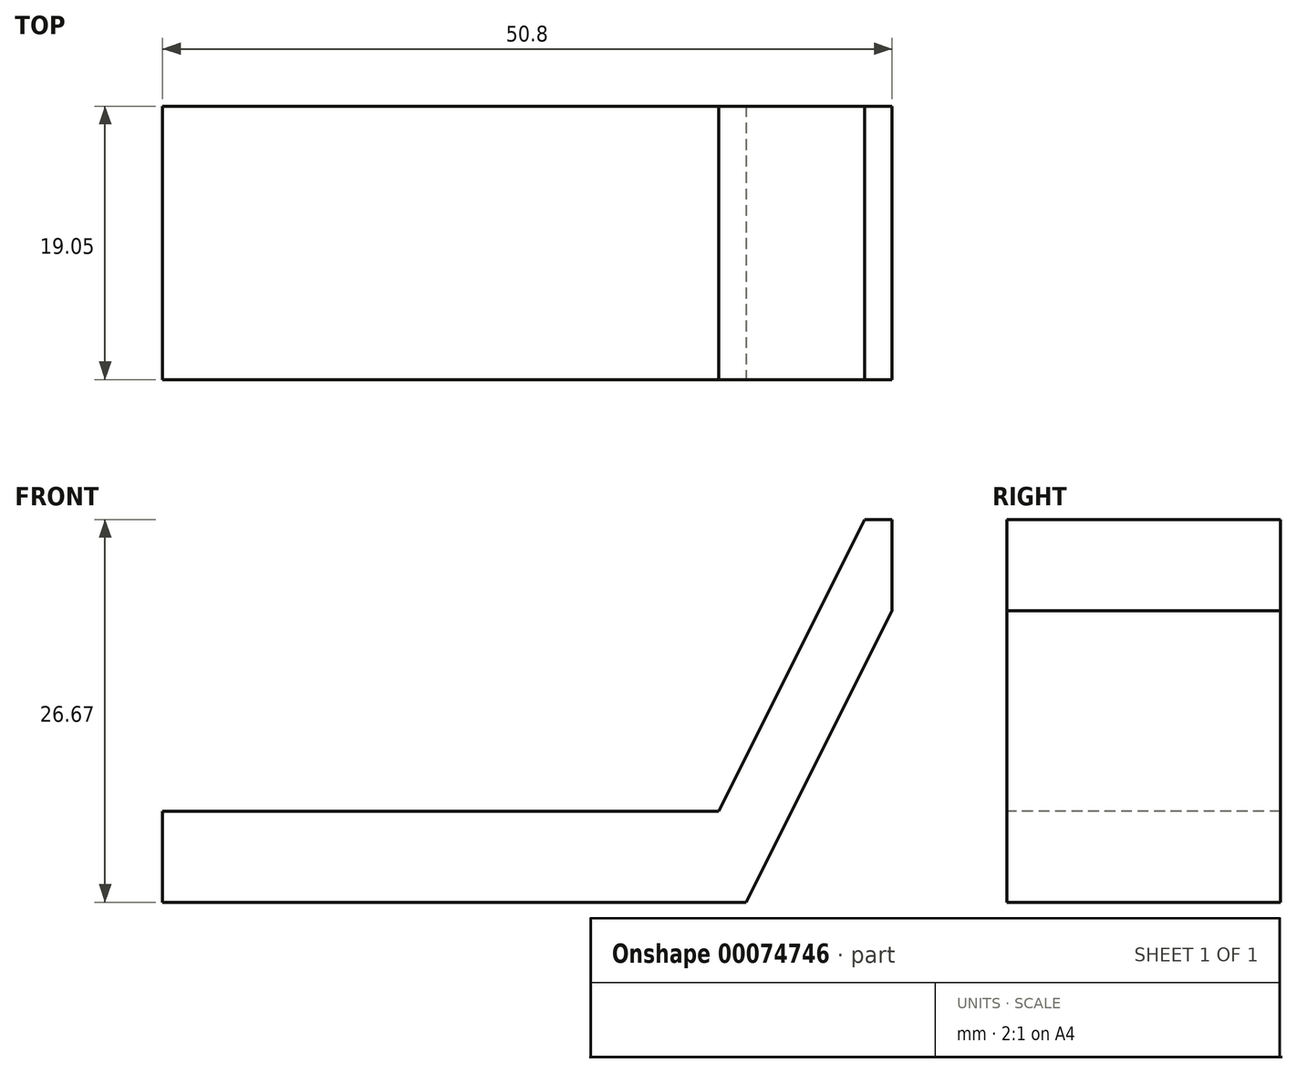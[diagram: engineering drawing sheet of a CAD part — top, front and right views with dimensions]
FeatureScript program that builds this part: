
annotation { "Feature Type Name" : "Feature", "Feature Type Description" : "" }
export const myFeature = defineFeature(function(context is Context, id is Id, definition is map)
    precondition{}
    {
        {
            var Q0;
            Q0=qCreatedBy(makeId("Front.planeOp"),FACE);
            var sketch = newSketch(context, id + "F0", { "sketchPlane" : qUnion([Q0])});
            skLineSegment(sketch, "E0", {"start": v(0, 0) * mm, "end": v(50.8, 0) * mm});
            skLineSegment(sketch, "E1", {"start": v(50.8, 0) * mm, "end": v(50.8, -6.35) * mm});
            skLineSegment(sketch, "E2", {"start": v(50.8, -6.35) * mm, "end": v(0, -6.35) * mm});
            skLineSegment(sketch, "E3", {"start": v(0, 0) * mm, "end": v(0, -6.35) * mm});
            skSolve(sketch);
        }
        {
            var Q0;
            Q0 = qSketchRegion(id + "F0", true);
            extrude(context, id + "F1", {"entities" : qUnion([Q0]), "depth" : 19.05 * mm});
        }
        {
            var Q0;
            Q0=makeQuery(id+"F1.opExtrude","SWEPT_FACE",FACE,{"disambiguationData":[OSD([sQuery(id+"F0.wireOp",EDGE,"E0")])]});
            var sketch = newSketch(context, id + "F2", { "sketchPlane" : qUnion([Q0])});
            skLineSegment(sketch, "E4", {"start": v(38.74, 0) * mm, "end": v(38.74, -19.05) * mm});
            skSolve(sketch);
        }
        {
            var Q0;
            {var subQ0=sQuery(id+"F2.wireOp",EDGE,"E4");Q0=makeQuery(id+"F2.imprint","IMPRINT",FACE,{"disambiguationData":[TD([[makeQuery(id+"F2.imprint","IMPRINT",EDGE,{"derivedFrom":subQ0}),1.0]])]});}
            extrude(context, id + "F3", {"entities" : qUnion([Q0]), "operationType" : NewBodyOperationType.ADD, "depth" : 20.32 * mm});
        }
        {
            var Q0;
            Q0=makeQuery(id+"F1.opExtrude","SWEPT_EDGE",EDGE,{"disambiguationData":[OSD([sQuery(id+"F0.wireOp",EDGE,"E1"),sQuery(id+"F0.wireOp",EDGE,"E2")])]});
            chamfer(context, id + "F4", {"entities" : qUnion([Q0]), "chamferType" : ChamferType.TWO_OFFSETS, "width1" : 20.32 * mm, "oppositeDirection" : false, "width2" : 10.16 * mm, "tangentPropagation" : true});
        }
        {
            var Q0;
            Q0=makeQuery(id+"F3.opExtrude","CAP_EDGE",EDGE,{"disambiguationData":[OSD([sQuery(id+"F2.wireOp",EDGE,"E4")])],"isStart":false});
            chamfer(context, id + "F5", {"entities" : qUnion([Q0]), "chamferType" : ChamferType.TWO_OFFSETS, "width1" : 10.16 * mm, "oppositeDirection" : false, "width2" : 20.32 * mm, "tangentPropagation" : true});
        }
    });
